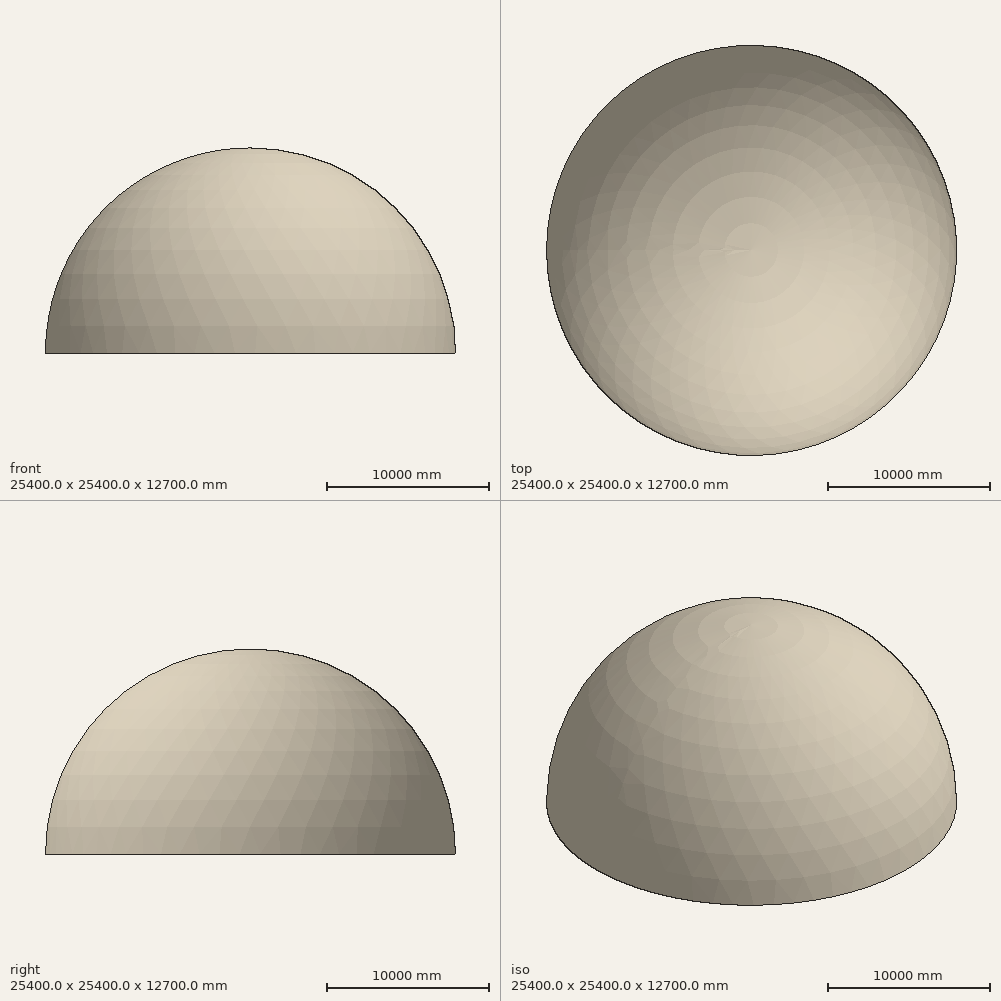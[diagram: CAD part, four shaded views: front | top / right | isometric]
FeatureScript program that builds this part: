
annotation { "Feature Type Name" : "Feature", "Feature Type Description" : "" }
export const myFeature = defineFeature(function(context is Context, id is Id, definition is map)
    precondition{}
    {
        {
            var Q0;
            Q0=qCreatedBy(makeId("Front.planeOp"),FACE);
            var sketch = newSketch(context, id + "F0", { "sketchPlane" : qUnion([Q0])});
            skArc(sketch, "E0", {"start": v(-12700, 0) * mm, "mid": v(-8980.26, 8980.26) * mm, "end": v(0, 12700) * mm});
            skArc(sketch, "E1", {"start": v(-12573, 0) * mm, "mid": v(-8890.45, 8890.45) * mm, "end": v(0, 12573) * mm});
            skLineSegment(sketch, "E2", {"start": v(-12700, 0) * mm, "end": v(-12573, 0) * mm});
            skLineSegment(sketch, "E3", {"start": v(0, 12700) * mm, "end": v(0, 12573) * mm});
            skLineSegment(sketch, "E4", {"start": v(0, 0) * mm, "end": v(0, 16895.03) * mm, "construction": true});
            skSolve(sketch);
        }
        {
            var Q0;
            Q0=qSketchRegion(id+"F0",true);
            var Q1;
            Q1=sQuery(id+"F0.wireOp",EDGE,"E4");
            revolve(context, id + "F1", {"entities" : qUnion([Q0]), "axis" : qUnion([Q1]), "revolveType" : RevolveType.FULL});
        }
    });
